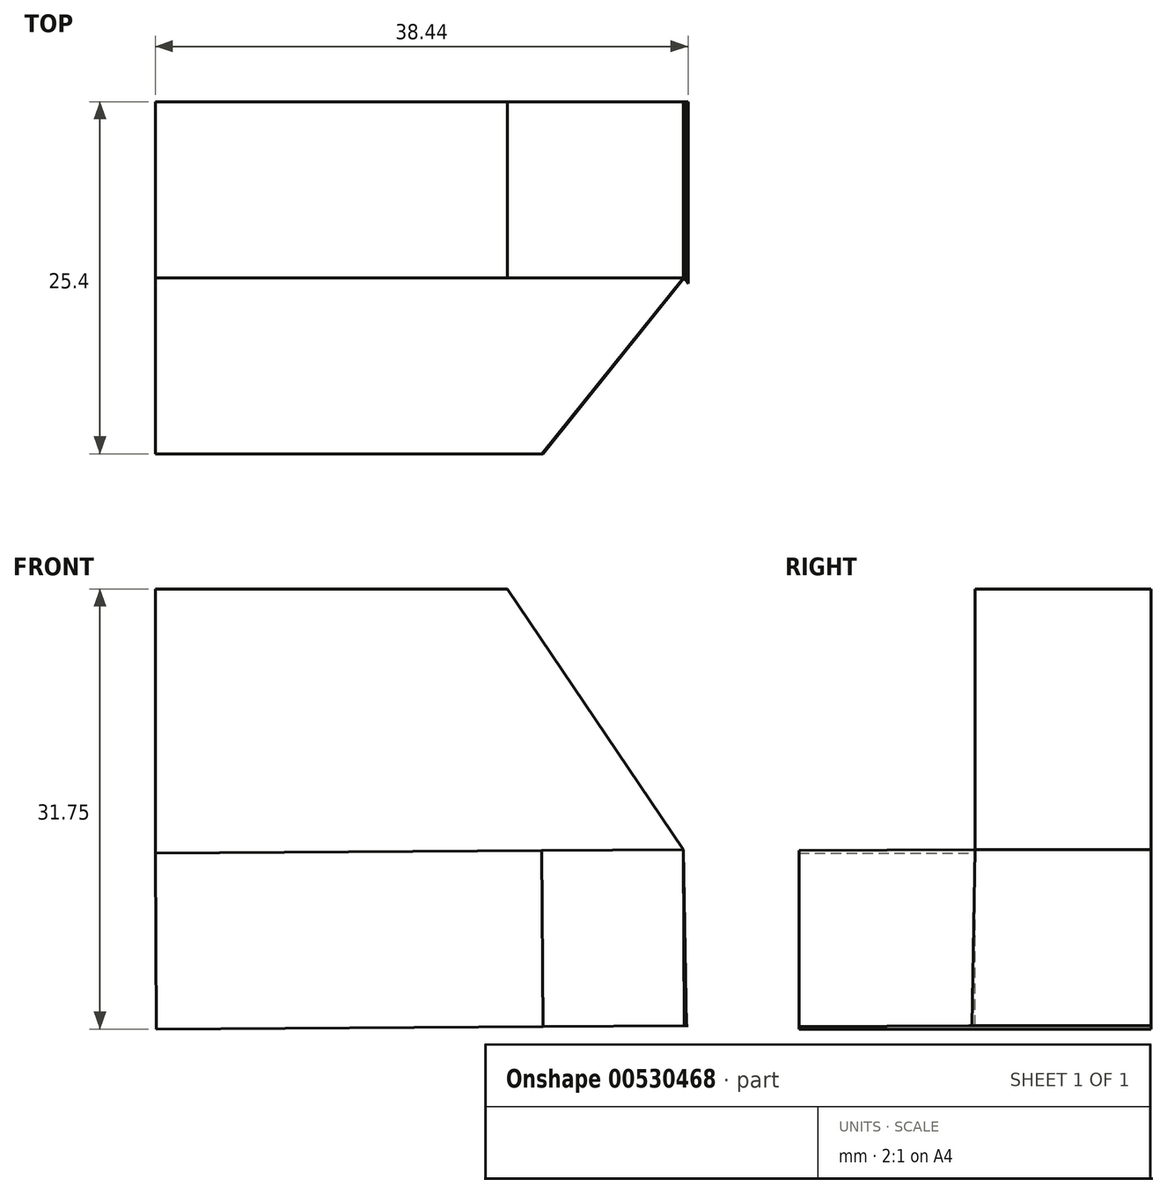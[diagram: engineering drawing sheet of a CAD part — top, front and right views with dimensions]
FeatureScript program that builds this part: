
annotation { "Feature Type Name" : "Feature", "Feature Type Description" : "" }
export const myFeature = defineFeature(function(context is Context, id is Id, definition is map)
    precondition{}
    {
        {
            var Q0;
            Q0=qCreatedBy(makeId("Front.planeOp"),FACE);
            var sketch = newSketch(context, id + "F0", { "sketchPlane" : qUnion([Q0])});
            skLineSegment(sketch, "E0", {"start": v(-50.98, 28.07) * mm, "end": v(-50.98, 47.12) * mm});
            skLineSegment(sketch, "E1", {"start": v(-50.98, 47.12) * mm, "end": v(-25.58, 47.12) * mm});
            skLineSegment(sketch, "E2", {"start": v(-25.58, 47.12) * mm, "end": v(-12.88, 28.31) * mm});
            skLineSegment(sketch, "E3", {"start": v(-12.88, 28.31) * mm, "end": v(-50.98, 28.07) * mm});
            skLineSegment(sketch, "E4", {"start": v(-50.98, 28.07) * mm, "end": v(-50.9, 15.37) * mm});
            skLineSegment(sketch, "E5", {"start": v(-50.9, 15.37) * mm, "end": v(-12.54, 15.62) * mm});
            skLineSegment(sketch, "E6", {"start": v(-12.66, 15.62) * mm, "end": v(-12.54, 15.62) * mm});
            skLineSegment(sketch, "E7", {"start": v(-12.66, 15.62) * mm, "end": v(-12.88, 28.31) * mm});
            skSolve(sketch);
        }
        {
            var Q0;
            Q0=makeQuery(id+"F0.imprint","IMPRINT",FACE,{"disambiguationData":[TD([[makeQuery(id+"F0.imprint","IMPRINT",EDGE,{"derivedFrom":sQuery(id+"F0.wireOp",EDGE,"E0")}),-1.0]])]});
            extrude(context, id + "F1", {"entities" : qUnion([Q0]), "depth" : 12.7 * mm, "offsetDistance" : 25.4 * mm});
        }
        {
            var Q0;
            Q0=makeQuery(id+"F0.imprint","IMPRINT",FACE,{"disambiguationData":[TD([[makeQuery(id+"F0.imprint","IMPRINT",EDGE,{"derivedFrom":sQuery(id+"F0.wireOp",EDGE,"E3")}),1.0]])]});
            extrude(context, id + "F2", {"entities" : qUnion([Q0]), "operationType" : NewBodyOperationType.ADD, "depth" : 25.4 * mm, "offsetDistance" : 25.4 * mm});
        }
        {
            var Q0;
            Q0=makeQuery(id+"F2.opExtrude","SWEPT_FACE",FACE,{"disambiguationData":[OSD([sQuery(id+"F0.wireOp",EDGE,"E3")])]});
            var sketch = newSketch(context, id + "F3", { "sketchPlane" : qUnion([Q0])});
            skLineSegment(sketch, "E8", {"start": v(-12.7, -12.7) * mm, "end": v(-22.92, -25.4) * mm});
            skLineSegment(sketch, "E9", {"start": v(-22.92, -25.4) * mm, "end": v(-4.62, -25.4) * mm});
            skLineSegment(sketch, "E10", {"start": v(-4.62, -25.4) * mm, "end": v(-12.7, -12.7) * mm});
            skSolve(sketch);
        }
        {
            var Q0;
            {var subQ0=sQuery(id+"F3.wireOp",EDGE,"E8");Q0=makeQuery(id+"F3.imprint","IMPRINT",FACE,{"disambiguationData":[TD([[makeQuery(id+"F3.imprint","IMPRINT",EDGE,{"derivedFrom":subQ0}),1.0]])]});}
            var Q1;
            {var subQ2=sQuery(id+"F3.wireOp",EDGE,"E10");Q1=makeQuery(id+"F3.imprint","IMPRINT",FACE,{"disambiguationData":[TD([[makeQuery(id+"F3.imprint","IMPRINT",EDGE,{"derivedFrom":subQ2}),1.0]])]});}
            extrude(context, id + "F4", {"entities" : qUnion([Q0, Q1]), "operationType" : NewBodyOperationType.REMOVE, "endBound" : BoundingType.THROUGH_ALL, "oppositeDirection" : true, "depth" : 25.4 * mm, "offsetDistance" : 25.4 * mm});
        }
    });
